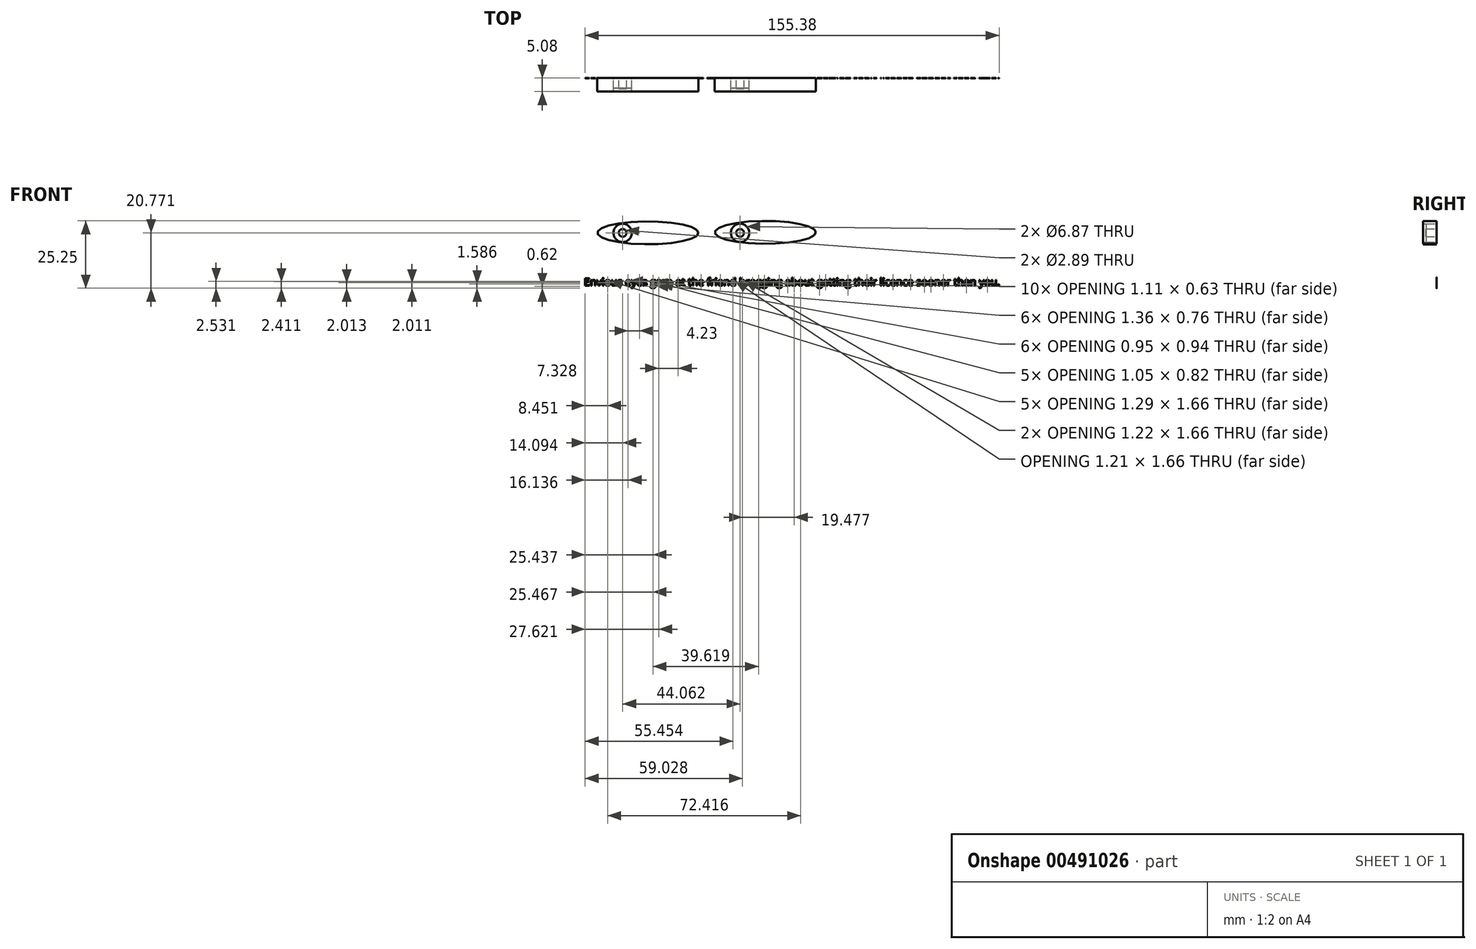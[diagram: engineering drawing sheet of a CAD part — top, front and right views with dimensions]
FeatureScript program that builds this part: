
annotation { "Feature Type Name" : "Feature", "Feature Type Description" : "" }
export const myFeature = defineFeature(function(context is Context, id is Id, definition is map)
    precondition{}
    {
        {
            var Q0;
            Q0=qCreatedBy(makeId("Front.planeOp"),FACE);
            var sketch = newSketch(context, id + "F0", { "sketchPlane" : qUnion([Q0])});
            skEllipse(sketch, "E0", {"center": v(-36.5, 16.96) * mm, "majorRadius": 18.99 * mm, "minorRadius": 4.3 * mm, "majorAxis": v(1, 0)});
            skEllipse(sketch, "E1", {"center": v(7.56, 17.15) * mm, "majorRadius": 18.99 * mm, "minorRadius": 4.3 * mm, "majorAxis": v(1, 0)});
            skCircle(sketch, "E2", {"center": v(-46, 16.96) * mm, "radius": 3.43 * mm});
            skCircle(sketch, "E3", {"center": v(-1.93, 16.96) * mm, "radius": 3.43 * mm});
            skCircle(sketch, "E4", {"center": v(-46, 16.96) * mm, "radius": 1.44 * mm});
            skCircle(sketch, "E5", {"center": v(-1.93, 16.96) * mm, "radius": 1.44 * mm});
            skSolve(sketch);
        }
        {
            var Q0;
            Q0 = qSketchRegion(id + "F0", true);
            extrude(context, id + "F1", {"entities" : qUnion([Q0]), "depth" : 5.08 * mm});
        }
        {
            var Q0;
            Q0=makeQuery(id+"F0.imprint","IMPRINT",FACE,{"disambiguationData":[TD([[makeQuery(id+"F0.imprint","IMPRINT",EDGE,{"derivedFrom":sQuery(id+"F0.wireOp",EDGE,"E2")}),1.0]])]});
            var Q1;
            Q1=makeQuery(id+"F0.imprint","IMPRINT",FACE,{"disambiguationData":[TD([[makeQuery(id+"F0.imprint","IMPRINT",EDGE,{"derivedFrom":sQuery(id+"F0.wireOp",EDGE,"E3")}),1.0]])]});
            extrude(context, id + "F2", {"entities" : qUnion([Q0, Q1]), "depth" : 3.8 * mm});
        }
        {
            var Q0;
            Q0=makeQuery(id+"F0.imprint","IMPRINT",FACE,{"disambiguationData":[TD([[makeQuery(id+"F0.imprint","IMPRINT",EDGE,{"derivedFrom":sQuery(id+"F0.wireOp",EDGE,"E4")}),1.0]])]});
            var Q1;
            Q1=makeQuery(id+"F0.imprint","IMPRINT",FACE,{"disambiguationData":[TD([[makeQuery(id+"F0.imprint","IMPRINT",EDGE,{"derivedFrom":sQuery(id+"F0.wireOp",EDGE,"E5")}),1.0]])]});
            extrude(context, id + "F3", {"entities" : qUnion([Q0, Q1]), "depth" : 4.06 * mm});
        }
        {
            var Q0;
            Q0=qCreatedBy(makeId("Front.planeOp"),FACE);
            var sketch = newSketch(context, id + "F4", { "sketchPlane" : qUnion([Q0])});
            skText(sketch, "E6", { "text": "Envious eyes gaze at the friend bragging about getting their licence sooner than you.  ", "fontName": "OpenSans-Regular.ttf"});
            const initialGuessF4  = {"E6": [-0.06048, -0.00286, 1, 0, 0.00286]};
            skSetInitialGuess(sketch, initialGuessF4);
            skSolve(sketch);
        }
        {
            var Q0;
            Q0 = qSketchRegion(id + "F4", true);
            extrude(context, id + "F5", {"entities" : qUnion([Q0]), "depth" : 0.05 * mm});
        }
    });
